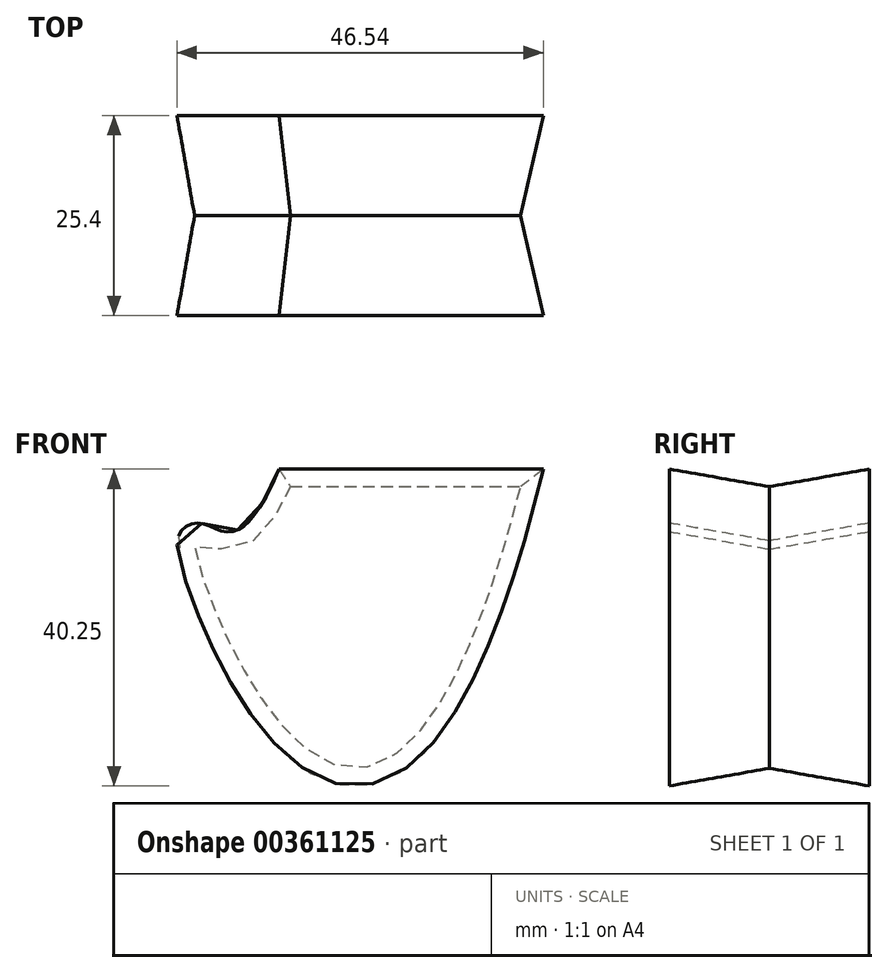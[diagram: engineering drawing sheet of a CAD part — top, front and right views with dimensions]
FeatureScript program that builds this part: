
annotation { "Feature Type Name" : "Feature", "Feature Type Description" : "" }
export const myFeature = defineFeature(function(context is Context, id is Id, definition is map)
    precondition{}
    {
        {
            var Q0;
            Q0=qCreatedBy(makeId("Front.planeOp"),FACE);
            var sketch = newSketch(context, id + "F0", { "sketchPlane" : qUnion([Q0])});
            skFitSpline(sketch, "E0", {"points": [v(-28.63, 0) * mm, v(-40.73, -8.05) * mm, v(0.62, 0) * mm], "startDerivative": vector(-53.49, -121.44) * mm, "endDerivative": vector(85.86, 337.4) * mm});
            skLineSegment(sketch, "E1", {"start": v(-28.63, 0) * mm, "end": v(0.62, 0) * mm});
            skSolve(sketch);
        }
        {
            var Q0;
            Q0=makeQuery(id+"F0.imprint","IMPRINT",FACE,{"disambiguationData":[TD([[makeQuery(id+"F0.imprint","IMPRINT",EDGE,{"derivedFrom":sQuery(id+"F0.wireOp",EDGE,"E0")}),1.0]])]});
            extrude(context, id + "F1", {"entities" : qUnion([Q0]), "endBound" : BoundingType.SYMMETRIC, "depth" : 25.4 * mm, "hasDraft" : true, "draftAngle" : 10 * degree});
        }
    });
